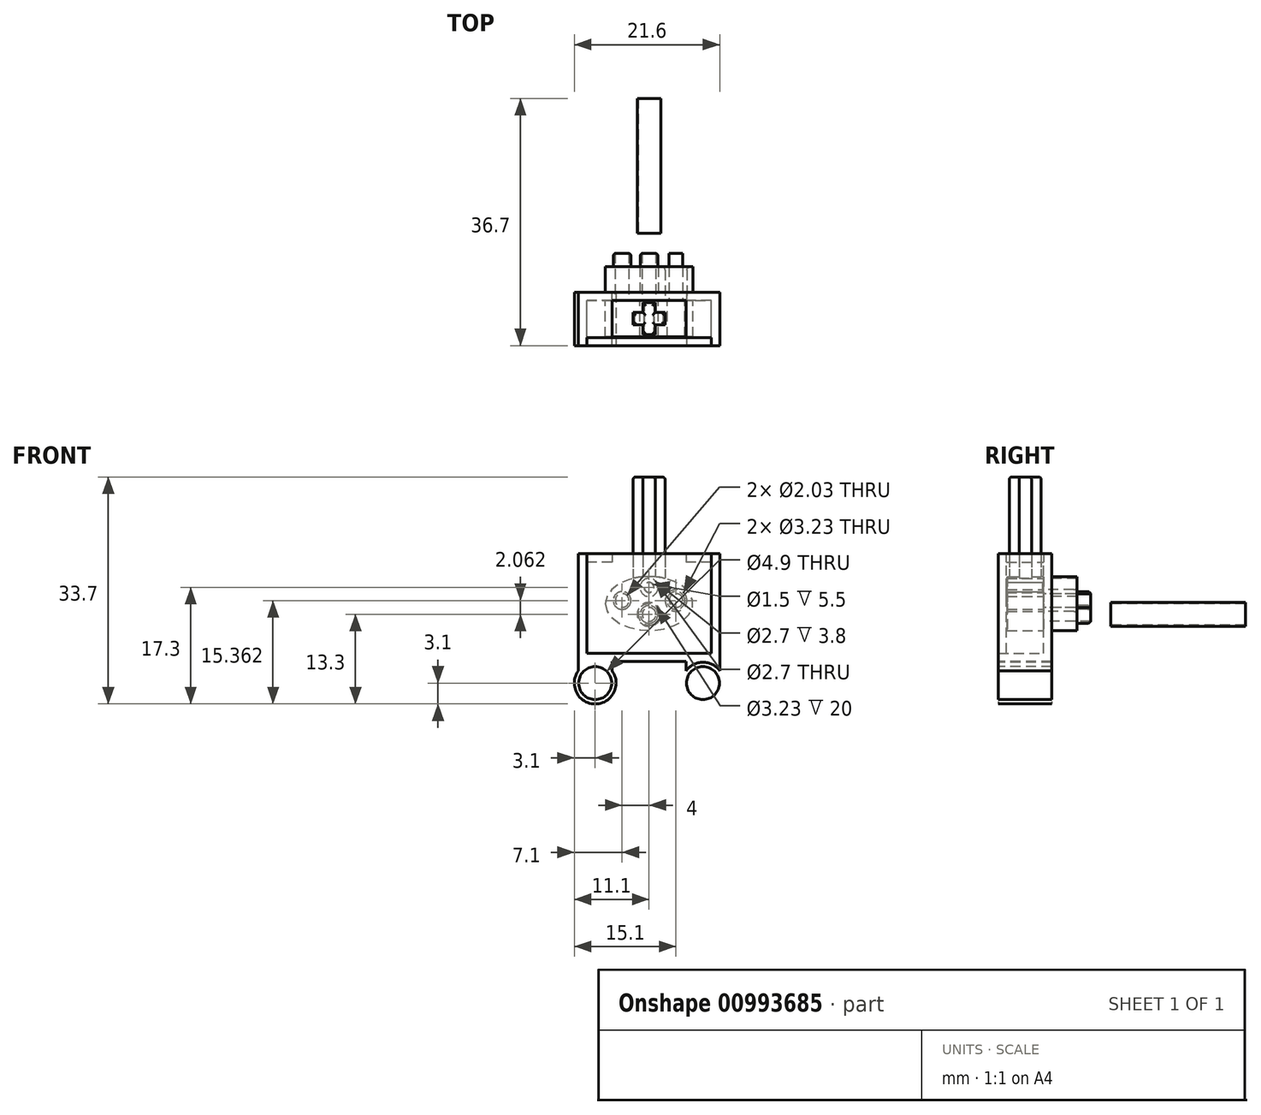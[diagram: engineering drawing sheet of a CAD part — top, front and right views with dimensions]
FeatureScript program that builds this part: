
annotation { "Feature Type Name" : "Feature", "Feature Type Description" : "" }
export const myFeature = defineFeature(function(context is Context, id is Id, definition is map)
    precondition{}
    {
        {
            var Q0;
            Q0=qCreatedBy(makeId("Front.planeOp"),FACE);
            var sketch = newSketch(context, id + "F0", { "sketchPlane" : qUnion([Q0])});
            skLineSegment(sketch, "E0", {"start": v(0, 5) * mm, "end": v(-10.5, 5) * mm});
            skLineSegment(sketch, "E1", {"start": v(-10.5, 5) * mm, "end": v(-10.5, -11) * mm});
            skLineSegment(sketch, "E2", {"start": v(-10.5, -11) * mm, "end": v(10.5, -11) * mm});
            skLineSegment(sketch, "E3", {"start": v(10.5, -11) * mm, "end": v(10.5, 5) * mm});
            skLineSegment(sketch, "E4", {"start": v(10.5, 5) * mm, "end": v(0, 5) * mm});
            skLineSegment(sketch, "E5", {"start": v(0, 5) * mm, "end": v(0, 0) * mm, "construction": true});
            skLineSegment(sketch, "E6.0", {"start": v(-9.25, 3.75) * mm, "end": v(-9.25, -9.75) * mm});
            skLineSegment(sketch, "E6.1", {"start": v(0, 3.75) * mm, "end": v(-9.25, 3.75) * mm});
            skLineSegment(sketch, "E6.2", {"start": v(-9.25, -9.75) * mm, "end": v(9.25, -9.75) * mm});
            skLineSegment(sketch, "E6.3", {"start": v(9.25, -9.75) * mm, "end": v(9.25, 3.75) * mm});
            skLineSegment(sketch, "E6.4", {"start": v(9.25, 3.75) * mm, "end": v(0, 3.75) * mm});
            skLineSegment(sketch, "E7", {"start": v(-5.5, 5) * mm, "end": v(-5.5, 3.75) * mm});
            skLineSegment(sketch, "E8.MirrorCS", {"start": v(5.5, 5) * mm, "end": v(5.5, 3.75) * mm});
            skLineSegment(sketch, "E9", {"start": v(0, -14.2) * mm, "end": v(-8, -14.2) * mm, "construction": true});
            skCircle(sketch, "E10", {"center": v(-8, -14.2) * mm, "radius": 2.45 * mm});
            skCircle(sketch, "E11.0", {"center": v(-8, -14.2) * mm, "radius": 3.1 * mm});
            skLineSegment(sketch, "E12.MirrorCS", {"start": v(0, -14.2) * mm, "end": v(8, -14.2) * mm, "construction": true});
            skCircle(sketch, "E13.MirrorC", {"center": v(8, -14.2) * mm, "radius": 2.45 * mm});
            skCircle(sketch, "E14.MirrorC", {"center": v(8, -14.2) * mm, "radius": 3.1 * mm});
            skLineSegment(sketch, "E15", {"start": v(-10.5, -11) * mm, "end": v(-10.5, -12.37) * mm});
            skLineSegment(sketch, "E16", {"start": v(-5.5, -11) * mm, "end": v(-5.5, -12.37) * mm});
            skLineSegment(sketch, "E17.MirrorCS", {"start": v(10.5, -11) * mm, "end": v(10.5, -12.37) * mm});
            skLineSegment(sketch, "E18.MirrorCS", {"start": v(5.5, -11) * mm, "end": v(5.5, -12.37) * mm});
            skLineSegment(sketch, "E19", {"start": v(-9.25, 3.75) * mm, "end": v(-9.25, 5) * mm});
            skLineSegment(sketch, "E20", {"start": v(9.25, 3.75) * mm, "end": v(9.25, 5) * mm});
            skCircle(sketch, "E21", {"center": v(0, 0) * mm, "radius": 0.75 * mm});
            skCircle(sketch, "E22.0", {"center": v(0, 0) * mm, "radius": 1.35 * mm});
            skCircle(sketch, "E23", {"center": v(0, -4) * mm, "radius": 1.62 * mm});
            skCircle(sketch, "E24", {"center": v(-4, -1.94) * mm, "radius": 1.62 * mm});
            skCircle(sketch, "E25.0", {"center": v(-4, -1.94) * mm, "radius": 1.02 * mm});
            skCircle(sketch, "E26.0", {"center": v(0, -4) * mm, "radius": 1.02 * mm});
            skCircle(sketch, "E27.MirrorC", {"center": v(4, -1.94) * mm, "radius": 1.62 * mm});
            skCircle(sketch, "E28.MirrorC", {"center": v(4, -1.94) * mm, "radius": 1.02 * mm});
            skCircle(sketch, "E29.0", {"center": v(0, -4) * mm, "radius": 1.32 * mm});
            skCircle(sketch, "E30.0", {"center": v(-4, -1.94) * mm, "radius": 1.32 * mm});
            skCircle(sketch, "E31.MirrorC", {"center": v(4, -1.94) * mm, "radius": 1.32 * mm});
            skLineSegment(sketch, "E32", {"start": v(0, 0) * mm, "end": v(0, -14.2) * mm, "construction": true});
            skEllipse(sketch, "E33", {"center": v(0, -2.39) * mm, "majorRadius": 6.5 * mm, "minorRadius": 4 * mm, "majorAxis": v(-1, 0)});
            skSolve(sketch);
        }
        {
            var Q0;
            {var subQ1=sQuery(id+"F0.wireOp",EDGE,"E6.0");Q0=makeQuery(id+"F0.imprint","IMPRINT",FACE,{"disambiguationData":[TD([[makeQuery(id+"F0.imprint","IMPRINT",EDGE,{"derivedFrom":subQ1}),1.0]])]});}
            var Q1;
            {var subQ8=sQuery(id+"F0.wireOp",EDGE,"E1");Q1=makeQuery(id+"F0.imprint","IMPRINT",FACE,{"disambiguationData":[TD([[makeQuery(id+"F0.imprint","IMPRINT",EDGE,{"derivedFrom":subQ8}),1.0]])]});}
            var Q2;
            {var subQ7=sQuery(id+"F0.wireOp",EDGE,"E7");Q2=makeQuery(id+"F0.imprint","IMPRINT",FACE,{"disambiguationData":[TD([[makeQuery(id+"F0.imprint","IMPRINT",EDGE,{"derivedFrom":subQ7}),1.0]])]});}
            var Q3;
            Q3=makeQuery(id+"F0.imprint","IMPRINT",FACE,{"disambiguationData":[TD([[makeQuery(id+"F0.imprint","IMPRINT",EDGE,{"derivedFrom":sQuery(id+"F0.wireOp",EDGE,"E10")}),-1.0]])]});
            var Q4;
            {var subQ0=sQuery(id+"F0.wireOp",EDGE,"E15");Q4=makeQuery(id+"F0.imprint","IMPRINT",FACE,{"disambiguationData":[TD([[makeQuery(id+"F0.imprint","IMPRINT",EDGE,{"derivedFrom":subQ0}),1.0]])]});}
            var Q5;
            Q5=makeQuery(id+"F0.imprint","IMPRINT",FACE,{"disambiguationData":[TD([[makeQuery(id+"F0.imprint","IMPRINT",EDGE,{"derivedFrom":sQuery(id+"F0.wireOp",EDGE,"E13.MirrorC")}),1.0]])]});
            var Q6;
            {var subQ0=sQuery(id+"F0.wireOp",EDGE,"E17.MirrorCS");Q6=makeQuery(id+"F0.imprint","IMPRINT",FACE,{"disambiguationData":[TD([[makeQuery(id+"F0.imprint","IMPRINT",EDGE,{"derivedFrom":subQ0}),-1.0]])]});}
            var Q7;
            {var subQ0=sQuery(id+"F0.wireOp",EDGE,"E7");Q7=makeQuery(id+"F0.imprint","IMPRINT",FACE,{"disambiguationData":[TD([[makeQuery(id+"F0.imprint","IMPRINT",EDGE,{"derivedFrom":subQ0}),-1.0]])]});}
            var Q8;
            {var subQ0=sQuery(id+"F0.wireOp",EDGE,"E8.MirrorCS");Q8=makeQuery(id+"F0.imprint","IMPRINT",FACE,{"disambiguationData":[TD([[makeQuery(id+"F0.imprint","IMPRINT",EDGE,{"derivedFrom":subQ0}),1.0]])]});}
            var Q9;
            Q9=makeQuery(id+"F0.imprint","IMPRINT",FACE,{"disambiguationData":[TD([[makeQuery(id+"F0.imprint","IMPRINT",EDGE,{"derivedFrom":sQuery(id+"F0.wireOp",EDGE,"E21")}),1.0]])]});
            var Q10;
            Q10=makeQuery(id+"F0.imprint","IMPRINT",FACE,{"disambiguationData":[TD([[makeQuery(id+"F0.imprint","IMPRINT",EDGE,{"derivedFrom":sQuery(id+"F0.wireOp",EDGE,"E21")}),-1.0]])]});
            var Q11;
            Q11=makeQuery(id+"F0.imprint","IMPRINT",FACE,{"disambiguationData":[TD([[makeQuery(id+"F0.imprint","IMPRINT",EDGE,{"derivedFrom":sQuery(id+"F0.wireOp",EDGE,"E24")}),1.0]])]});
            var Q12;
            Q12=makeQuery(id+"F0.imprint","IMPRINT",FACE,{"disambiguationData":[TD([[makeQuery(id+"F0.imprint","IMPRINT",EDGE,{"derivedFrom":sQuery(id+"F0.wireOp",EDGE,"E23")}),1.0]])]});
            var Q13;
            Q13=makeQuery(id+"F0.imprint","IMPRINT",FACE,{"disambiguationData":[TD([[makeQuery(id+"F0.imprint","IMPRINT",EDGE,{"derivedFrom":sQuery(id+"F0.wireOp",EDGE,"E27.MirrorC")}),-1.0]])]});
            var Q14;
            Q14=makeQuery(id+"F0.imprint","IMPRINT",FACE,{"disambiguationData":[TD([[makeQuery(id+"F0.imprint","IMPRINT",EDGE,{"derivedFrom":sQuery(id+"F0.wireOp",EDGE,"E22.0")}),-1.0]])]});
            var Q15;
            Q15=makeQuery(id+"F0.imprint","IMPRINT",FACE,{"disambiguationData":[TD([[makeQuery(id+"F0.imprint","IMPRINT",EDGE,{"derivedFrom":sQuery(id+"F0.wireOp",EDGE,"E28.MirrorC")}),1.0]])]});
            var Q16;
            Q16=makeQuery(id+"F0.imprint","IMPRINT",FACE,{"disambiguationData":[TD([[makeQuery(id+"F0.imprint","IMPRINT",EDGE,{"derivedFrom":sQuery(id+"F0.wireOp",EDGE,"E26.0")}),-1.0]])]});
            var Q17;
            Q17=makeQuery(id+"F0.imprint","IMPRINT",FACE,{"disambiguationData":[TD([[makeQuery(id+"F0.imprint","IMPRINT",EDGE,{"derivedFrom":sQuery(id+"F0.wireOp",EDGE,"E25.0")}),-1.0]])]});
            extrude(context, id + "F1", {"entities" : qUnion([Q0, Q1, Q2, Q3, Q4, Q5, Q6, Q7, Q8, Q9, Q10, Q11, Q12, Q13, Q14, Q15, Q16, Q17]), "oppositeDirection" : true, "depth" : 1.2 * mm, "offsetDistance" : 25 * mm});
        }
        {
            var Q0;
            {var subQ6=sQuery(id+"F0.wireOp",EDGE,"E1");Q0=makeQuery(id+"F0.imprint","IMPRINT",FACE,{"disambiguationData":[TD([[makeQuery(id+"F0.imprint","IMPRINT",EDGE,{"derivedFrom":subQ6}),1.0]])]});}
            var Q1;
            Q1=makeQuery(id+"F0.imprint","IMPRINT",FACE,{"disambiguationData":[TD([[makeQuery(id+"F0.imprint","IMPRINT",EDGE,{"derivedFrom":sQuery(id+"F0.wireOp",EDGE,"E10")}),-1.0]])]});
            var Q2;
            {var subQ0=sQuery(id+"F0.wireOp",EDGE,"E15");Q2=makeQuery(id+"F0.imprint","IMPRINT",FACE,{"disambiguationData":[TD([[makeQuery(id+"F0.imprint","IMPRINT",EDGE,{"derivedFrom":subQ0}),1.0]])]});}
            var Q3;
            Q3=makeQuery(id+"F0.imprint","IMPRINT",FACE,{"disambiguationData":[TD([[makeQuery(id+"F0.imprint","IMPRINT",EDGE,{"derivedFrom":sQuery(id+"F0.wireOp",EDGE,"E13.MirrorC")}),1.0]])]});
            var Q4;
            {var subQ0=sQuery(id+"F0.wireOp",EDGE,"E17.MirrorCS");Q4=makeQuery(id+"F0.imprint","IMPRINT",FACE,{"disambiguationData":[TD([[makeQuery(id+"F0.imprint","IMPRINT",EDGE,{"derivedFrom":subQ0}),-1.0]])]});}
            extrude(context, id + "F2", {"entities" : qUnion([Q0, Q1, Q2, Q3, Q4]), "operationType" : NewBodyOperationType.ADD, "depth" : (7.9 - 1.2) * mm, "offsetDistance" : 25 * mm});
        }
        {
            var Q0;
            {var subQ0=sQuery(id+"F0.wireOp",EDGE,"E7");Q0=makeQuery(id+"F0.imprint","IMPRINT",FACE,{"disambiguationData":[TD([[makeQuery(id+"F0.imprint","IMPRINT",EDGE,{"derivedFrom":subQ0}),-1.0]])]});}
            var Q1;
            {var subQ0=sQuery(id+"F0.wireOp",EDGE,"E8.MirrorCS");Q1=makeQuery(id+"F0.imprint","IMPRINT",FACE,{"disambiguationData":[TD([[makeQuery(id+"F0.imprint","IMPRINT",EDGE,{"derivedFrom":subQ0}),1.0]])]});}
            var Q2;
            Q2=makeQuery(id+"F0.imprint","IMPRINT",FACE,{"disambiguationData":[TD([[makeQuery(id+"F0.imprint","IMPRINT",EDGE,{"derivedFrom":sQuery(id+"F0.wireOp",EDGE,"E21")}),-1.0]])]});
            extrude(context, id + "F3", {"entities" : qUnion([Q0, Q1, Q2]), "operationType" : NewBodyOperationType.ADD, "depth" : (7.9 - 2.4) * mm, "offsetDistance" : 25 * mm});
        }
        {
            var Q0;
            Q0=makeQuery(id+"F0.imprint","IMPRINT",FACE,{"disambiguationData":[TD([[makeQuery(id+"F0.imprint","IMPRINT",EDGE,{"derivedFrom":sQuery(id+"F0.wireOp",EDGE,"E24")}),1.0]])]});
            var Q1;
            Q1=makeQuery(id+"F0.imprint","IMPRINT",FACE,{"disambiguationData":[TD([[makeQuery(id+"F0.imprint","IMPRINT",EDGE,{"derivedFrom":sQuery(id+"F0.wireOp",EDGE,"E23")}),1.0]])]});
            var Q2;
            Q2=makeQuery(id+"F0.imprint","IMPRINT",FACE,{"disambiguationData":[TD([[makeQuery(id+"F0.imprint","IMPRINT",EDGE,{"derivedFrom":sQuery(id+"F0.wireOp",EDGE,"E27.MirrorC")}),-1.0]])]});
            extrude(context, id + "F4", {"entities" : qUnion([Q0, Q1, Q2]), "operationType" : NewBodyOperationType.ADD, "oppositeDirection" : true, "depth" : 5 * mm, "offsetDistance" : 25 * mm});
        }
        {
            var Q0;
            Q0=makeQuery(id+"F0.imprint","IMPRINT",FACE,{"disambiguationData":[TD([[makeQuery(id+"F0.imprint","IMPRINT",EDGE,{"derivedFrom":sQuery(id+"F0.wireOp",EDGE,"E25.0")}),-1.0]])]});
            var Q1;
            Q1=makeQuery(id+"F0.imprint","IMPRINT",FACE,{"disambiguationData":[TD([[makeQuery(id+"F0.imprint","IMPRINT",EDGE,{"derivedFrom":sQuery(id+"F0.wireOp",EDGE,"E26.0")}),-1.0]])]});
            var Q2;
            Q2=makeQuery(id+"F0.imprint","IMPRINT",FACE,{"disambiguationData":[TD([[makeQuery(id+"F0.imprint","IMPRINT",EDGE,{"derivedFrom":sQuery(id+"F0.wireOp",EDGE,"E28.MirrorC")}),1.0]])]});
            extrude(context, id + "F5", {"entities" : qUnion([Q0, Q1, Q2]), "operationType" : NewBodyOperationType.ADD, "oppositeDirection" : true, "depth" : 7 * mm, "offsetDistance" : 25 * mm});
        }
        {
            var Q0;
            Q0=makeQuery(id+"F4.opExtrude","CAP_EDGE",EDGE,{"disambiguationData":[OSD([sQuery(id+"F0.wireOp",EDGE,"E27.MirrorC")])],"isStart":false});
            var Q1;
            Q1=makeQuery(id+"F4.opExtrude","CAP_EDGE",EDGE,{"disambiguationData":[OSD([sQuery(id+"F0.wireOp",EDGE,"E23")])],"isStart":false});
            var Q2;
            Q2=makeQuery(id+"F4.opExtrude","CAP_EDGE",EDGE,{"disambiguationData":[OSD([sQuery(id+"F0.wireOp",EDGE,"E24")])],"isStart":false});
            fillet(context, id + "F6", {"entities" : qUnion([Q0, Q1, Q2]), "radius" : 0.5 * mm, "tangentPropagation" : true, "allowEdgeOverflow" : false});
        }
        {
            var Q0;
            Q0=makeQuery(id+"F5.opExtrude","CAP_EDGE",EDGE,{"disambiguationData":[OSD([sQuery(id+"F0.wireOp",EDGE,"E31.MirrorC")])],"isStart":false});
            var Q1;
            Q1=makeQuery(id+"F5.opExtrude","CAP_EDGE",EDGE,{"disambiguationData":[OSD([sQuery(id+"F0.wireOp",EDGE,"E29.0")])],"isStart":false});
            var Q2;
            Q2=makeQuery(id+"F5.opExtrude","CAP_EDGE",EDGE,{"disambiguationData":[OSD([sQuery(id+"F0.wireOp",EDGE,"E30.0")])],"isStart":false});
            fillet(context, id + "F7", {"entities" : qUnion([Q0, Q1, Q2]), "radius" : 0.5 * mm, "tangentPropagation" : true, "allowEdgeOverflow" : false});
        }
        {
            var Q0;
            Q0=makeQuery(id+"F3.opExtrude","CAP_FACE",FACE,{"disambiguationData":[OSD([sQuery(id+"F0.wireOp",EDGE,"E0"),sQuery(id+"F0.wireOp",EDGE,"E6.1"),sQuery(id+"F0.wireOp",EDGE,"E7"),sQuery(id+"F0.wireOp",EDGE,"E19")])],"isStart":false});
            var sketch = newSketch(context, id + "F8", { "sketchPlane" : qUnion([Q0])});
            skLineSegment(sketch, "E34.0", {"start": v(-9.25, 5) * mm, "end": v(-9.25, -9.75) * mm});
            skLineSegment(sketch, "E35.0", {"start": v(-9.25, -9.75) * mm, "end": v(9.25, -9.75) * mm});
            skLineSegment(sketch, "E36.0", {"start": v(9.25, -9.75) * mm, "end": v(9.25, 5) * mm});
            skLineSegment(sketch, "E37.0", {"start": v(5.5, 5) * mm, "end": v(-5.5, 5) * mm});
            skLineSegment(sketch, "E38.0", {"start": v(-5.5, 5) * mm, "end": v(-9.25, 5) * mm});
            skLineSegment(sketch, "E39.0", {"start": v(9.25, 5) * mm, "end": v(5.5, 5) * mm});
            skCircle(sketch, "E40.0", {"center": v(0, 0) * mm, "radius": 0.72 * mm});
            skSolve(sketch);
        }
        {
            var Q0;
            Q0=qSketchRegion(id+"F8",true);
            var Q1;
            Q1=makeQuery(id+"F8.imprint","IMPRINT",FACE,{"disambiguationData":[TD([[makeQuery(id+"F8.imprint","IMPRINT",EDGE,{"derivedFrom":sQuery(id+"F8.wireOp",EDGE,"E40.0")}),1.0]])]});
            extrude(context, id + "F9", {"entities" : qUnion([Q0, Q1]), "depth" : 1.2 * mm, "offsetDistance" : 25 * mm});
        }
        {
            var Q0;
            Q0=makeQuery(id+"F8.imprint","IMPRINT",FACE,{"disambiguationData":[TD([[makeQuery(id+"F8.imprint","IMPRINT",EDGE,{"derivedFrom":sQuery(id+"F8.wireOp",EDGE,"E40.0")}),1.0]])]});
            extrude(context, id + "F10", {"entities" : qUnion([Q0]), "operationType" : NewBodyOperationType.ADD, "oppositeDirection" : true, "depth" : 5.4 * mm, "offsetDistance" : 25 * mm});
        }
        {
            var Q0;
            Q0=makeQuery(id+"F0.imprint","IMPRINT",FACE,{"disambiguationData":[TD([[makeQuery(id+"F0.imprint","IMPRINT",EDGE,{"derivedFrom":sQuery(id+"F0.wireOp",EDGE,"E22.0")}),-1.0]])]});
            var Q1;
            Q1=makeQuery(id+"F0.imprint","IMPRINT",FACE,{"disambiguationData":[TD([[makeQuery(id+"F0.imprint","IMPRINT",EDGE,{"derivedFrom":sQuery(id+"F0.wireOp",EDGE,"E24")}),1.0]])]});
            var Q2;
            Q2=makeQuery(id+"F0.imprint","IMPRINT",FACE,{"disambiguationData":[TD([[makeQuery(id+"F0.imprint","IMPRINT",EDGE,{"derivedFrom":sQuery(id+"F0.wireOp",EDGE,"E25.0")}),-1.0]])]});
            var Q3;
            Q3=makeQuery(id+"F0.imprint","IMPRINT",FACE,{"disambiguationData":[TD([[makeQuery(id+"F0.imprint","IMPRINT",EDGE,{"derivedFrom":sQuery(id+"F0.wireOp",EDGE,"E25.0")}),1.0]])]});
            var Q4;
            Q4=makeQuery(id+"F0.imprint","IMPRINT",FACE,{"disambiguationData":[TD([[makeQuery(id+"F0.imprint","IMPRINT",EDGE,{"derivedFrom":sQuery(id+"F0.wireOp",EDGE,"E23")}),1.0]])]});
            var Q5;
            Q5=makeQuery(id+"F0.imprint","IMPRINT",FACE,{"disambiguationData":[TD([[makeQuery(id+"F0.imprint","IMPRINT",EDGE,{"derivedFrom":sQuery(id+"F0.wireOp",EDGE,"E26.0")}),-1.0]])]});
            var Q6;
            Q6=makeQuery(id+"F0.imprint","IMPRINT",FACE,{"disambiguationData":[TD([[makeQuery(id+"F0.imprint","IMPRINT",EDGE,{"derivedFrom":sQuery(id+"F0.wireOp",EDGE,"E26.0")}),1.0]])]});
            var Q7;
            Q7=makeQuery(id+"F0.imprint","IMPRINT",FACE,{"disambiguationData":[TD([[makeQuery(id+"F0.imprint","IMPRINT",EDGE,{"derivedFrom":sQuery(id+"F0.wireOp",EDGE,"E27.MirrorC")}),-1.0]])]});
            var Q8;
            Q8=makeQuery(id+"F0.imprint","IMPRINT",FACE,{"disambiguationData":[TD([[makeQuery(id+"F0.imprint","IMPRINT",EDGE,{"derivedFrom":sQuery(id+"F0.wireOp",EDGE,"E28.MirrorC")}),1.0]])]});
            var Q9;
            Q9=makeQuery(id+"F0.imprint","IMPRINT",FACE,{"disambiguationData":[TD([[makeQuery(id+"F0.imprint","IMPRINT",EDGE,{"derivedFrom":sQuery(id+"F0.wireOp",EDGE,"E28.MirrorC")}),-1.0]])]});
            extrude(context, id + "F11", {"entities" : qUnion([Q0, Q1, Q2, Q3, Q4, Q5, Q6, Q7, Q8, Q9]), "depth" : 5.4 * mm, "offsetDistance" : 25 * mm});
        }
        {
            var Q0;
            Q0=qCreatedBy(makeId("Top.planeOp"),FACE);
            cPlane(context, id + "F12", {"entities" : qUnion([Q0]), "cplaneType" : CPlaneType.OFFSET, "offset" : 1.4 * mm, "width" : 150 * mm, "height" : 150 * mm});
        }
        {
            var Q0;
            Q0=qCreatedBy(id+"F12.planeOp",FACE);
            var sketch = newSketch(context, id + "F13", { "sketchPlane" : qUnion([Q0])});
            skLineSegment(sketch, "E41.0", {"start": v(6.5, -5.4) * mm, "end": v(-6.5, -5.4) * mm, "construction": true});
            skLineSegment(sketch, "E42.0", {"start": v(6.5, 0) * mm, "end": v(-6.5, 0) * mm, "construction": true});
            skLineSegment(sketch, "E43", {"start": v(-6.5, 0) * mm, "end": v(-6.5, -5.4) * mm, "construction": true});
            skLineSegment(sketch, "E44", {"start": v(6.5, 0) * mm, "end": v(6.5, -5.4) * mm, "construction": true});
            skLineSegment(sketch, "E45", {"start": v(-6.5, -2.7) * mm, "end": v(6.5, -2.7) * mm, "construction": true});
            skLineSegment(sketch, "E46", {"start": v(0, 0) * mm, "end": v(0, -2.7) * mm, "construction": true});
            skLineSegment(sketch, "E47", {"start": v(0, -2.7) * mm, "end": v(0, -5.4) * mm, "construction": true});
            skLineSegment(sketch, "E48", {"start": v(0, -0.33) * mm, "end": v(-0.92, -0.33) * mm});
            skLineSegment(sketch, "E49", {"start": v(-0.92, -0.33) * mm, "end": v(-0.92, -1.78) * mm});
            skLineSegment(sketch, "E50", {"start": v(-0.92, -1.78) * mm, "end": v(-2.38, -1.78) * mm});
            skLineSegment(sketch, "E51", {"start": v(-2.38, -1.78) * mm, "end": v(-2.38, -2.7) * mm});
            skLineSegment(sketch, "E52.MirrorCS", {"start": v(2.38, -1.78) * mm, "end": v(2.38, -2.7) * mm});
            skLineSegment(sketch, "E53.MirrorCS", {"start": v(0.92, -1.78) * mm, "end": v(2.38, -1.78) * mm});
            skLineSegment(sketch, "E54.MirrorCS", {"start": v(0, -0.33) * mm, "end": v(0.92, -0.33) * mm});
            skLineSegment(sketch, "E55.MirrorCS", {"start": v(0.92, -0.33) * mm, "end": v(0.92, -1.78) * mm});
            skLineSegment(sketch, "E56.MirrorCS", {"start": v(0.92, -5.07) * mm, "end": v(0.92, -3.62) * mm});
            skLineSegment(sketch, "E57.MirrorCS", {"start": v(0.92, -3.62) * mm, "end": v(2.38, -3.62) * mm});
            skLineSegment(sketch, "E58.MirrorCS", {"start": v(2.38, -3.62) * mm, "end": v(2.38, -2.7) * mm});
            skLineSegment(sketch, "E59.MirrorCS", {"start": v(-2.38, -3.62) * mm, "end": v(-2.38, -2.7) * mm});
            skLineSegment(sketch, "E60.MirrorCS", {"start": v(-0.92, -3.62) * mm, "end": v(-2.38, -3.62) * mm});
            skLineSegment(sketch, "E61.MirrorCS", {"start": v(-0.92, -5.07) * mm, "end": v(-0.92, -3.62) * mm});
            skLineSegment(sketch, "E62.MirrorCS", {"start": v(0, -5.07) * mm, "end": v(-0.92, -5.07) * mm});
            skLineSegment(sketch, "E63.MirrorCS", {"start": v(0, -5.07) * mm, "end": v(0.92, -5.07) * mm});
            skLineSegment(sketch, "E64.0", {"start": v(0.75, 0) * mm, "end": v(-0.75, 0) * mm});
            skSolve(sketch);
        }
        {
            var Q0;
            Q0=makeQuery(id+"F13.imprint","IMPRINT",FACE,{"disambiguationData":[TD([[makeQuery(id+"F13.imprint","IMPRINT",EDGE,{"derivedFrom":sQuery(id+"F13.wireOp",EDGE,"E49")}),1.0]])]});
            extrude(context, id + "F14", {"entities" : qUnion([Q0]), "operationType" : NewBodyOperationType.ADD, "depth" : 15 * mm, "offsetDistance" : 25 * mm});
        }
        {
            var Q0;
            Q0=makeQuery(id+"F14.opExtrude","CAP_FACE",FACE,{"disambiguationData":[OSD([sQuery(id+"F13.wireOp",EDGE,"E49"),sQuery(id+"F13.wireOp",EDGE,"E50"),sQuery(id+"F13.wireOp",EDGE,"E51"),sQuery(id+"F13.wireOp",EDGE,"E52.MirrorCS"),sQuery(id+"F13.wireOp",EDGE,"E53.MirrorCS"),sQuery(id+"F13.wireOp",EDGE,"E55.MirrorCS"),sQuery(id+"F13.wireOp",EDGE,"E54.MirrorCS"),sQuery(id+"F13.wireOp",EDGE,"E48"),sQuery(id+"F13.wireOp",EDGE,"E56.MirrorCS"),sQuery(id+"F13.wireOp",EDGE,"E57.MirrorCS"),sQuery(id+"F13.wireOp",EDGE,"E58.MirrorCS"),sQuery(id+"F13.wireOp",EDGE,"E59.MirrorCS"),sQuery(id+"F13.wireOp",EDGE,"E60.MirrorCS"),sQuery(id+"F13.wireOp",EDGE,"E61.MirrorCS"),sQuery(id+"F13.wireOp",EDGE,"E62.MirrorCS"),sQuery(id+"F13.wireOp",EDGE,"E63.MirrorCS")])],"isStart":false});
            fillet(context, id + "F15", {"entities" : qUnion([Q0]), "radius" : 0.4 * mm, "tangentPropagation" : true, "allowEdgeOverflow" : false});
        }
        {
            var Q0;
            Q0=qCreatedBy(makeId("Front.planeOp"),FACE);
            cPlane(context, id + "F16", {"entities" : qUnion([Q0]), "cplaneType" : CPlaneType.OFFSET, "offset" : 10 * mm, "oppositeDirection" : true, "width" : 150 * mm, "height" : 150 * mm});
        }
        {
            var Q0;
            Q0=qCreatedBy(id+"F16.planeOp",FACE);
            var sketch = newSketch(context, id + "F17", { "sketchPlane" : qUnion([Q0])});
            skCircle(sketch, "E65.0", {"center": v(0, -4) * mm, "radius": 1.62 * mm});
            skCircle(sketch, "E66.0", {"center": v(0, -4) * mm, "radius": 1.77 * mm});
            skSolve(sketch);
        }
        {
            var Q0;
            Q0=makeQuery(id+"F17.imprint","IMPRINT",FACE,{"disambiguationData":[TD([[makeQuery(id+"F17.imprint","IMPRINT",EDGE,{"derivedFrom":sQuery(id+"F17.wireOp",EDGE,"E65.0")}),-1.0]])]});
            var Q1;
            Q1=sQuery(id+"F17.wireOp",EDGE,"E65.0");
            extrude(context, id + "F18", {"entities" : qUnion([Q0]), "surfaceEntities" : qUnion([Q1]), "oppositeDirection" : true, "depth" : 20 * mm, "offsetDistance" : 25 * mm});
        }
    });
